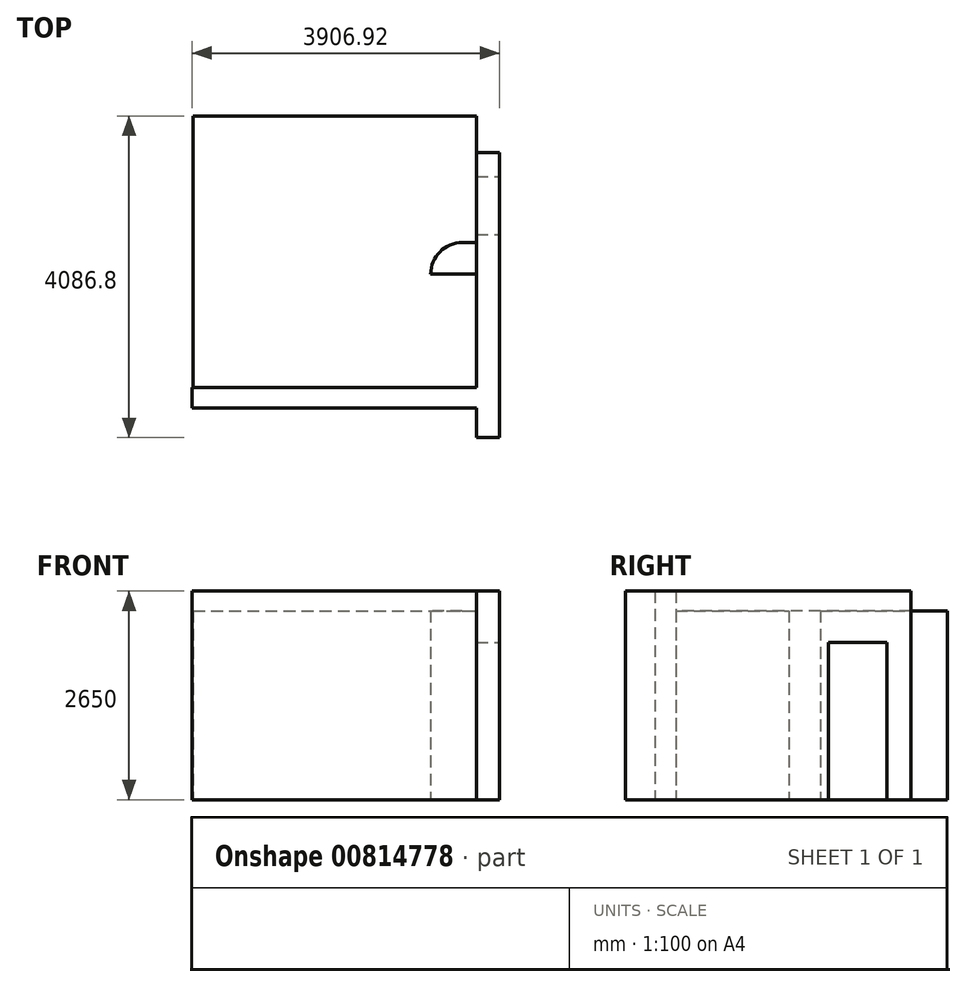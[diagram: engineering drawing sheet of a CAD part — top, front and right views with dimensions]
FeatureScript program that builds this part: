
annotation { "Feature Type Name" : "Feature", "Feature Type Description" : "" }
export const myFeature = defineFeature(function(context is Context, id is Id, definition is map)
    precondition{}
    {
        {
            var Q0;
            Q0=qCreatedBy(makeId("Top.planeOp"),FACE);
            var sketch = newSketch(context, id + "F0", { "sketchPlane" : qUnion([Q0])});
            skLineSegment(sketch, "E0.bottom", {"start": v(0, 0) * mm, "end": v(5550, 0) * mm});
            skLineSegment(sketch, "E0.top", {"start": v(0, 6900) * mm, "end": v(5550, 6900) * mm});
            skLineSegment(sketch, "E0.left", {"start": v(0, 0) * mm, "end": v(0, 6900) * mm});
            skLineSegment(sketch, "E0.right", {"start": v(5550, 0) * mm, "end": v(5550, 6900) * mm});
            skLineSegment(sketch, "E1", {"start": v(0, 3450) * mm, "end": v(5550, 3450) * mm});
            skLineSegment(sketch, "E2", {"start": v(1950, 6900) * mm, "end": v(1950, 3450) * mm});
            skLineSegment(sketch, "E3", {"start": v(4150, 6900) * mm, "end": v(4150, 5060) * mm});
            skLineSegment(sketch, "E4", {"start": v(4150, 5060) * mm, "end": v(1950, 5060) * mm});
            skPoint(sketch, "E4.endSnap0", {"position": v(1950, 5175) * mm});
            skLineSegment(sketch, "E5.bottom", {"start": v(4530, 3450) * mm, "end": v(5550, 3450) * mm});
            skLineSegment(sketch, "E5.top", {"start": v(4950, 4290) * mm, "end": v(5550, 4290) * mm});
            skLineSegment(sketch, "E5.left", {"start": v(4530, 3450) * mm, "end": v(4530, 3870) * mm});
            skLineSegment(sketch, "E5.right", {"start": v(5550, 3450) * mm, "end": v(5550, 4290) * mm});
            skLineSegment(sketch, "E6", {"start": v(4950, 4290) * mm, "end": v(4530, 3870) * mm});
            skLineSegment(sketch, "E7.bottom", {"start": v(3350, 3450) * mm, "end": v(4250, 3450) * mm});
            skLineSegment(sketch, "E7.top", {"start": v(3350, 3350) * mm, "end": v(4250, 3350) * mm});
            skLineSegment(sketch, "E7.left", {"start": v(3350, 3450) * mm, "end": v(3350, 3350) * mm});
            skLineSegment(sketch, "E7.right", {"start": v(4250, 3450) * mm, "end": v(4250, 3350) * mm});
            skLineSegment(sketch, "E8.bottom", {"start": v(4950, 4890) * mm, "end": v(5550, 4890) * mm});
            skLineSegment(sketch, "E8.left", {"start": v(4950, 4890) * mm, "end": v(4950, 4290) * mm});
            skLineSegment(sketch, "E8.right", {"start": v(5550, 4890) * mm, "end": v(5550, 4290) * mm});
            skPoint(sketch, "E9", {"position": v(5550, 5160) * mm});
            skLineSegment(sketch, "E10.bottom", {"start": v(1950, 3450) * mm, "end": v(2790, 3450) * mm});
            skLineSegment(sketch, "E10.top", {"start": v(1950, 3920) * mm, "end": v(2790, 3920) * mm});
            skLineSegment(sketch, "E10.left", {"start": v(1950, 3450) * mm, "end": v(1950, 3920) * mm});
            skLineSegment(sketch, "E10.right", {"start": v(2790, 3450) * mm, "end": v(2790, 3920) * mm});
            skLineSegment(sketch, "E11.bottom", {"start": v(4530, 3450) * mm, "end": v(4230, 3450) * mm});
            skLineSegment(sketch, "E11.top", {"start": v(4530, 3870) * mm, "end": v(4230, 3870) * mm});
            skLineSegment(sketch, "E11.right", {"start": v(4230, 3450) * mm, "end": v(4230, 3870) * mm});
            skLineSegment(sketch, "E12.bottom", {"start": v(2790, 3450) * mm, "end": v(3390, 3450) * mm});
            skLineSegment(sketch, "E12.top", {"start": v(2790, 3880) * mm, "end": v(3390, 3880) * mm});
            skLineSegment(sketch, "E12.left", {"start": v(2790, 3450) * mm, "end": v(2790, 3880) * mm});
            skLineSegment(sketch, "E12.right", {"start": v(3390, 3450) * mm, "end": v(3390, 3880) * mm});
            skLineSegment(sketch, "E13.top", {"start": v(4970, 4890) * mm, "end": v(5550, 4890) * mm});
            skLineSegment(sketch, "E13.right", {"start": v(5550, 5290) * mm, "end": v(5550, 4890) * mm});
            skPoint(sketch, "E14", {"position": v(5370, 4890) * mm});
            skArc(sketch, "E15", {"start": v(4970, 4890) * mm, "mid": v(5087.16, 5172.84) * mm, "end": v(5370, 5290) * mm});
            skLineSegment(sketch, "E16", {"start": v(5370, 5290) * mm, "end": v(5550, 5290) * mm});
            skSolve(sketch);
        }
        {
            var Q0;
            {var subQ6=sQuery(id+"F0.wireOp",EDGE,"E10.top");Q0=makeQuery(id+"F0.imprint","IMPRINT",FACE,{"disambiguationData":[TD([[makeQuery(id+"F0.imprint","IMPRINT",EDGE,{"derivedFrom":subQ6}),-1.0]])]});}
            var Q1;
            {var subQ0=sQuery(id+"F0.wireOp",EDGE,"E12.top");Q1=makeQuery(id+"F0.imprint","IMPRINT",FACE,{"disambiguationData":[TD([[makeQuery(id+"F0.imprint","IMPRINT",EDGE,{"derivedFrom":subQ0}),-1.0]])]});}
            var Q2;
            {var subQ0=sQuery(id+"F0.wireOp",EDGE,"E5.left");Q2=makeQuery(id+"F0.imprint","IMPRINT",FACE,{"disambiguationData":[TD([[makeQuery(id+"F0.imprint","IMPRINT",EDGE,{"derivedFrom":subQ0}),1.0]])]});}
            var Q3;
            {var subQ1=sQuery(id+"F0.wireOp",EDGE,"E5.top");Q3=makeQuery(id+"F0.imprint","IMPRINT",FACE,{"disambiguationData":[TD([[makeQuery(id+"F0.imprint","IMPRINT",EDGE,{"derivedFrom":subQ1}),-1.0]])]});}
            var Q4;
            {var subQ3=sQuery(id+"F0.wireOp",EDGE,"E5.top");Q4=makeQuery(id+"F0.imprint","IMPRINT",FACE,{"disambiguationData":[TD([[makeQuery(id+"F0.imprint","IMPRINT",EDGE,{"derivedFrom":subQ3}),1.0]])]});}
            var Q5;
            {var subQ4=sQuery(id+"F0.wireOp",EDGE,"E15");Q5=makeQuery(id+"F0.imprint","IMPRINT",FACE,{"disambiguationData":[TD([[makeQuery(id+"F0.imprint","IMPRINT",EDGE,{"derivedFrom":subQ4}),-1.0]])]});}
            var Q6;
            {var subQ3=sQuery(id+"F0.wireOp",EDGE,"E3");Q6=makeQuery(id+"F0.imprint","IMPRINT",FACE,{"disambiguationData":[TD([[makeQuery(id+"F0.imprint","IMPRINT",EDGE,{"derivedFrom":subQ3}),-1.0]])]});}
            extrude(context, id + "F1", {"entities" : qUnion([Q0, Q1, Q2, Q3, Q4, Q5, Q6]), "depth" : 2400 * mm, "offsetDistance" : 25 * mm});
        }
        {
            var Q0;
            Q0=makeQuery(id+"F1.opExtrude","CAP_FACE",FACE,{"disambiguationData":[OSD([sQuery(id+"F0.wireOp",EDGE,"E0.right"),sQuery(id+"F0.wireOp",EDGE,"E1"),sQuery(id+"F0.wireOp",EDGE,"E6"),sQuery(id+"F0.wireOp",EDGE,"E8.bottom"),sQuery(id+"F0.wireOp",EDGE,"E8.left"),sQuery(id+"F0.wireOp",EDGE,"E11.top"),sQuery(id+"F0.wireOp",EDGE,"E11.right"),sQuery(id+"F0.wireOp",EDGE,"E15"),sQuery(id+"F0.wireOp",EDGE,"E16")])],"isStart":true});
            var sketch = newSketch(context, id + "F2", { "sketchPlane" : qUnion([Q0])});
            skLineSegment(sketch, "E17.bottom", {"start": v(1938.31, -3450) * mm, "end": v(5550, -3450) * mm});
            skLineSegment(sketch, "E17.top", {"start": v(1938.31, -3185.52) * mm, "end": v(5550, -3185.52) * mm});
            skLineSegment(sketch, "E17.left", {"start": v(1938.31, -3450) * mm, "end": v(1938.31, -3185.52) * mm});
            skLineSegment(sketch, "E17.right", {"start": v(5550, -3450) * mm, "end": v(5550, -3185.52) * mm});
            skLineSegment(sketch, "E18.bottom", {"start": v(5845.23, -6435.97) * mm, "end": v(5550, -6435.97) * mm});
            skLineSegment(sketch, "E18.top", {"start": v(5845.23, -2813.2) * mm, "end": v(5550, -2813.2) * mm});
            skLineSegment(sketch, "E18.left", {"start": v(5845.23, -6435.97) * mm, "end": v(5845.23, -2813.2) * mm});
            skLineSegment(sketch, "E18.right", {"start": v(5550, -6435.97) * mm, "end": v(5550, -2813.2) * mm});
            skSolve(sketch);
        }
        {
            var Q0;
            {var subQ2=sQuery(id+"F2.wireOp",EDGE,"E18.bottom");Q0=makeQuery(id+"F2.imprint","IMPRINT",FACE,{"disambiguationData":[TD([[makeQuery(id+"F2.imprint","IMPRINT",EDGE,{"derivedFrom":subQ2}),-1.0]])]});}
            var Q1;
            {var subQ1=sQuery(id+"F2.wireOp",EDGE,"E17.top");Q1=makeQuery(id+"F2.imprint","IMPRINT",FACE,{"disambiguationData":[TD([[makeQuery(id+"F2.imprint","IMPRINT",EDGE,{"derivedFrom":subQ1}),-1.0]])]});}
            extrude(context, id + "F3", {"entities" : qUnion([Q0, Q1]), "oppositeDirection" : true, "depth" : 2650 * mm, "offsetDistance" : 25 * mm});
        }
        {
            var Q0;
            Q0=makeQuery(id+"F3.opExtrude","CAP_FACE",FACE,{"disambiguationData":[OSD([sQuery(id+"F2.wireOp",EDGE,"E17.bottom"),sQuery(id+"F2.wireOp",EDGE,"E17.top"),sQuery(id+"F2.wireOp",EDGE,"E17.left"),sQuery(id+"F2.wireOp",EDGE,"E18.bottom"),sQuery(id+"F2.wireOp",EDGE,"E18.top"),sQuery(id+"F2.wireOp",EDGE,"E18.left"),sQuery(id+"F2.wireOp",EDGE,"E18.right")])],"isStart":true});
            var sketch = newSketch(context, id + "F4", { "sketchPlane" : qUnion([Q0])});
            skLineSegment(sketch, "E19.bottom", {"start": v(5413.9, -6130) * mm, "end": v(5965.4, -6130) * mm});
            skLineSegment(sketch, "E19.top", {"start": v(5413.9, -5390) * mm, "end": v(5965.4, -5390) * mm});
            skLineSegment(sketch, "E19.left", {"start": v(5413.9, -6130) * mm, "end": v(5413.9, -5390) * mm});
            skLineSegment(sketch, "E19.right", {"start": v(5965.4, -6130) * mm, "end": v(5965.4, -5390) * mm});
            skSolve(sketch);
        }
        {
            var Q0;
            {var subQ0=sQuery(id+"F4.wireOp",EDGE,"E19.bottom");var subQ5=makeQuery(id+"F3.opExtrude","CAP_EDGE",EDGE,{"disambiguationData":[OSD([sQuery(id+"F2.wireOp",EDGE,"E18.left")])],"isStart":true});var subQ6=makeQuery(id+"F4.imprint","INTERSECT",VERTEX,{"derivedFrom":[subQ5,subQ0]});Q0=makeQuery(id+"F4.imprint","IMPRINT",FACE,{"disambiguationData":[TD([[makeQuery(id+"F4.imprint","IMPRINT",EDGE,{"disambiguationData":[TD([[subQ6,-1.0]])],"derivedFrom":subQ5}),1.0]])]});}
            extrude(context, id + "F5", {"entities" : qUnion([Q0]), "operationType" : NewBodyOperationType.REMOVE, "oppositeDirection" : true, "depth" : 2000 * mm, "offsetDistance" : 25 * mm});
        }
    });
